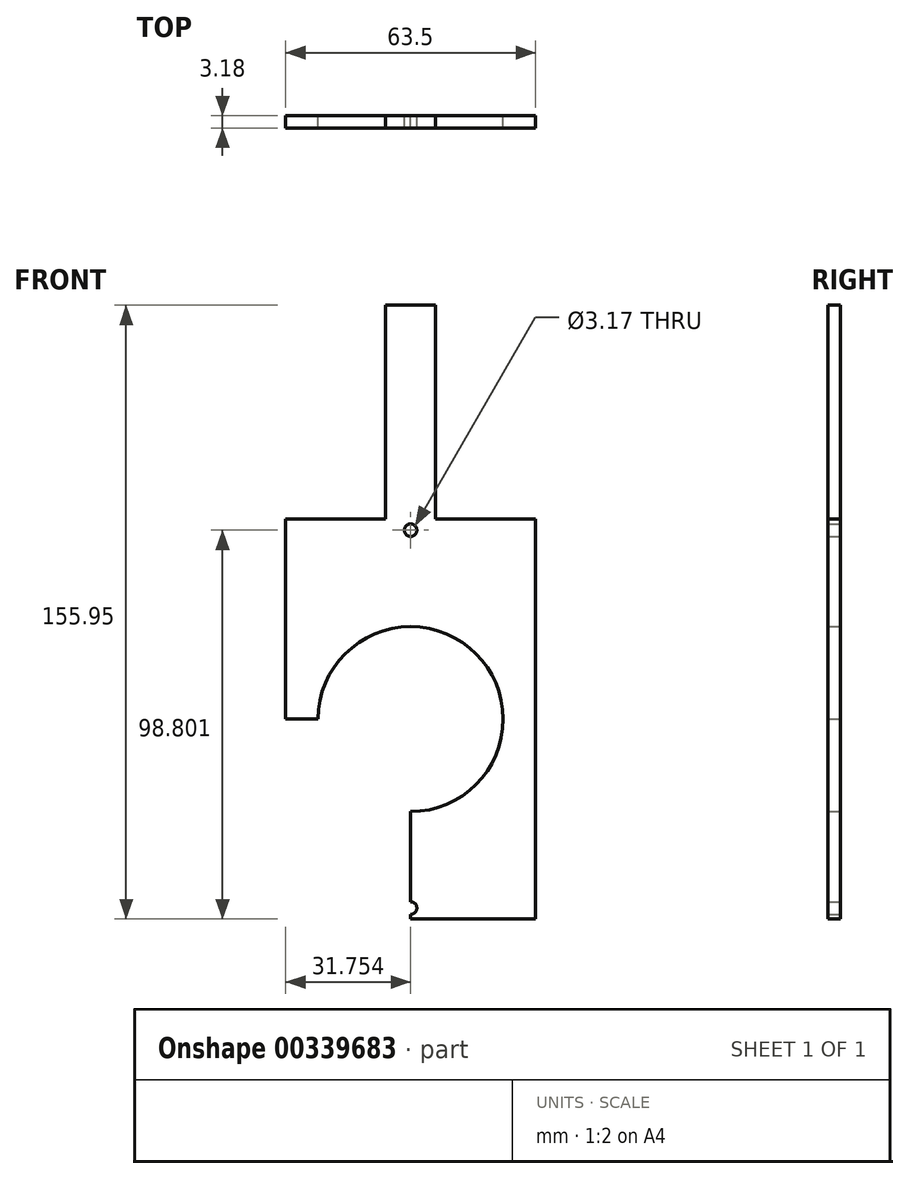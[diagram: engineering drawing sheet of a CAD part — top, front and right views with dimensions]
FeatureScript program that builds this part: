
annotation { "Feature Type Name" : "Feature", "Feature Type Description" : "" }
export const myFeature = defineFeature(function(context is Context, id is Id, definition is map)
    precondition{}
    {
        {
            var Q0;
            Q0=qCreatedBy(makeId("Front.planeOp"),FACE);
            var sketch = newSketch(context, id + "F0", { "sketchPlane" : qUnion([Q0])});
            skLineSegment(sketch, "E0.bottom", {"start": v(-123.45, 108) * mm, "end": v(-56.78, 108) * mm});
            skLineSegment(sketch, "E0.top", {"start": v(-120.28, 6.4) * mm, "end": v(-56.78, 6.4) * mm});
            skLineSegment(sketch, "E0.right", {"start": v(-56.78, 108) * mm, "end": v(-56.78, 6.4) * mm});
            skCircle(sketch, "E1", {"center": v(-88.53, 105.2) * mm, "radius": 1.59 * mm});
            skCircle(sketch, "E2", {"center": v(-88.53, 9.2) * mm, "radius": 1.59 * mm});
            skLineSegment(sketch, "E3", {"start": v(-121.86, 57.2) * mm, "end": v(-66.08, 57.2) * mm});
            skLineSegment(sketch, "E4", {"start": v(-88.53, 6.4) * mm, "end": v(-88.53, 108) * mm});
            skLineSegment(sketch, "E5.right", {"start": v(-120.28, 108) * mm, "end": v(-120.28, 6.4) * mm});
            skLineSegment(sketch, "E6.bottom", {"start": v(-94.88, 108) * mm, "end": v(-82.18, 108) * mm});
            skLineSegment(sketch, "E6.top", {"start": v(-94.88, 162.35) * mm, "end": v(-82.18, 162.35) * mm});
            skLineSegment(sketch, "E6.left", {"start": v(-94.88, 108) * mm, "end": v(-94.88, 162.35) * mm});
            skLineSegment(sketch, "E6.right", {"start": v(-82.18, 108) * mm, "end": v(-82.18, 162.35) * mm});
            skCircle(sketch, "E7", {"center": v(-88.53, 57.2) * mm, "radius": 23.5 * mm});
            skSolve(sketch);
        }
        {
            var Q0;
            {var subQ0=sQuery(id+"F0.wireOp",EDGE,"E4");var subQ3=sQuery(id+"F0.wireOp",EDGE,"E1");var subQ4=makeQuery(id+"F0.imprint","INTERSECT",VERTEX,{"disambiguationData":[OD(0.0)],"derivedFrom":[subQ3,subQ0]});Q0=makeQuery(id+"F0.imprint","IMPRINT",FACE,{"disambiguationData":[TD([[makeQuery(id+"F0.imprint","IMPRINT",EDGE,{"disambiguationData":[TD([[subQ4,1.0]])],"derivedFrom":subQ3}),-1.0]])]});}
            var Q1;
            {var subQ0=sQuery(id+"F0.wireOp",EDGE,"E0.right");Q1=makeQuery(id+"F0.imprint","IMPRINT",FACE,{"disambiguationData":[TD([[makeQuery(id+"F0.imprint","IMPRINT",EDGE,{"derivedFrom":subQ0}),-1.0]])]});}
            var Q2;
            {var subQ0=sQuery(id+"F0.wireOp",EDGE,"E4");var subQ3=sQuery(id+"F0.wireOp",EDGE,"E2");var subQ4=makeQuery(id+"F0.imprint","INTERSECT",VERTEX,{"disambiguationData":[OD(0.0)],"derivedFrom":[subQ3,subQ0]});Q2=makeQuery(id+"F0.imprint","IMPRINT",FACE,{"disambiguationData":[TD([[makeQuery(id+"F0.imprint","IMPRINT",EDGE,{"disambiguationData":[TD([[subQ4,1.0]])],"derivedFrom":subQ3}),-1.0]])]});}
            var Q3;
            Q3=makeQuery(id+"F0.imprint","IMPRINT",FACE,{"disambiguationData":[TD([[makeQuery(id+"F0.imprint","IMPRINT",EDGE,{"derivedFrom":sQuery(id+"F0.wireOp",EDGE,"E6.top")}),-1.0]])]});
            var Q4;
            Q4=makeQuery(id+"F0.imprint","IMPRINT",FACE,{"disambiguationData":[TD([[makeQuery(id+"F0.imprint","IMPRINT",EDGE,{"derivedFrom":sQuery(id+"F0.wireOp",EDGE,"f7b349f1-b396-4a21-881e-e5968fab744d0.MirrorCS")}),1.0]])]});
            var Q5;
            {var subQ0=sQuery(id+"F0.wireOp",EDGE,"E5.top");Q5=makeQuery(id+"F0.imprint","IMPRINT",FACE,{"disambiguationData":[TD([[makeQuery(id+"F0.imprint","IMPRINT",EDGE,{"derivedFrom":subQ0}),-1.0]])]});}
            var Q6;
            {var subQ0=sQuery(id+"F0.wireOp",EDGE,"E5.bottom");Q6=makeQuery(id+"F0.imprint","IMPRINT",FACE,{"disambiguationData":[TD([[makeQuery(id+"F0.imprint","IMPRINT",EDGE,{"derivedFrom":subQ0}),1.0]])]});}
            var Q7;
            {var subQ0=sQuery(id+"F0.wireOp",EDGE,"ba0b4900-d1d3-49b5-b7f6-abc080a1aacb4.MirrorCS");Q7=makeQuery(id+"F0.imprint","IMPRINT",FACE,{"disambiguationData":[TD([[makeQuery(id+"F0.imprint","IMPRINT",EDGE,{"derivedFrom":subQ0}),-1.0]])]});}
            var Q8;
            Q8=makeQuery(id+"F0.imprint","IMPRINT",FACE,{"disambiguationData":[TD([[makeQuery(id+"F0.imprint","IMPRINT",EDGE,{"derivedFrom":sQuery(id+"F0.wireOp",EDGE,"E0.right")}),1.0]])]});
            var Q9;
            {var subQ0=sQuery(id+"F0.wireOp",EDGE,"ba0b4900-d1d3-49b5-b7f6-abc080a1aacb1.MirrorCS");Q9=makeQuery(id+"F0.imprint","IMPRINT",FACE,{"disambiguationData":[TD([[makeQuery(id+"F0.imprint","IMPRINT",EDGE,{"derivedFrom":subQ0}),1.0]])]});}
            extrude(context, id + "F1", {"entities" : qUnion([Q0, Q1, Q2, Q3, Q4, Q5, Q6, Q7, Q8, Q9]), "depth" : 3.17 * mm, "offsetDistance" : 25.4 * mm});
        }
    });
